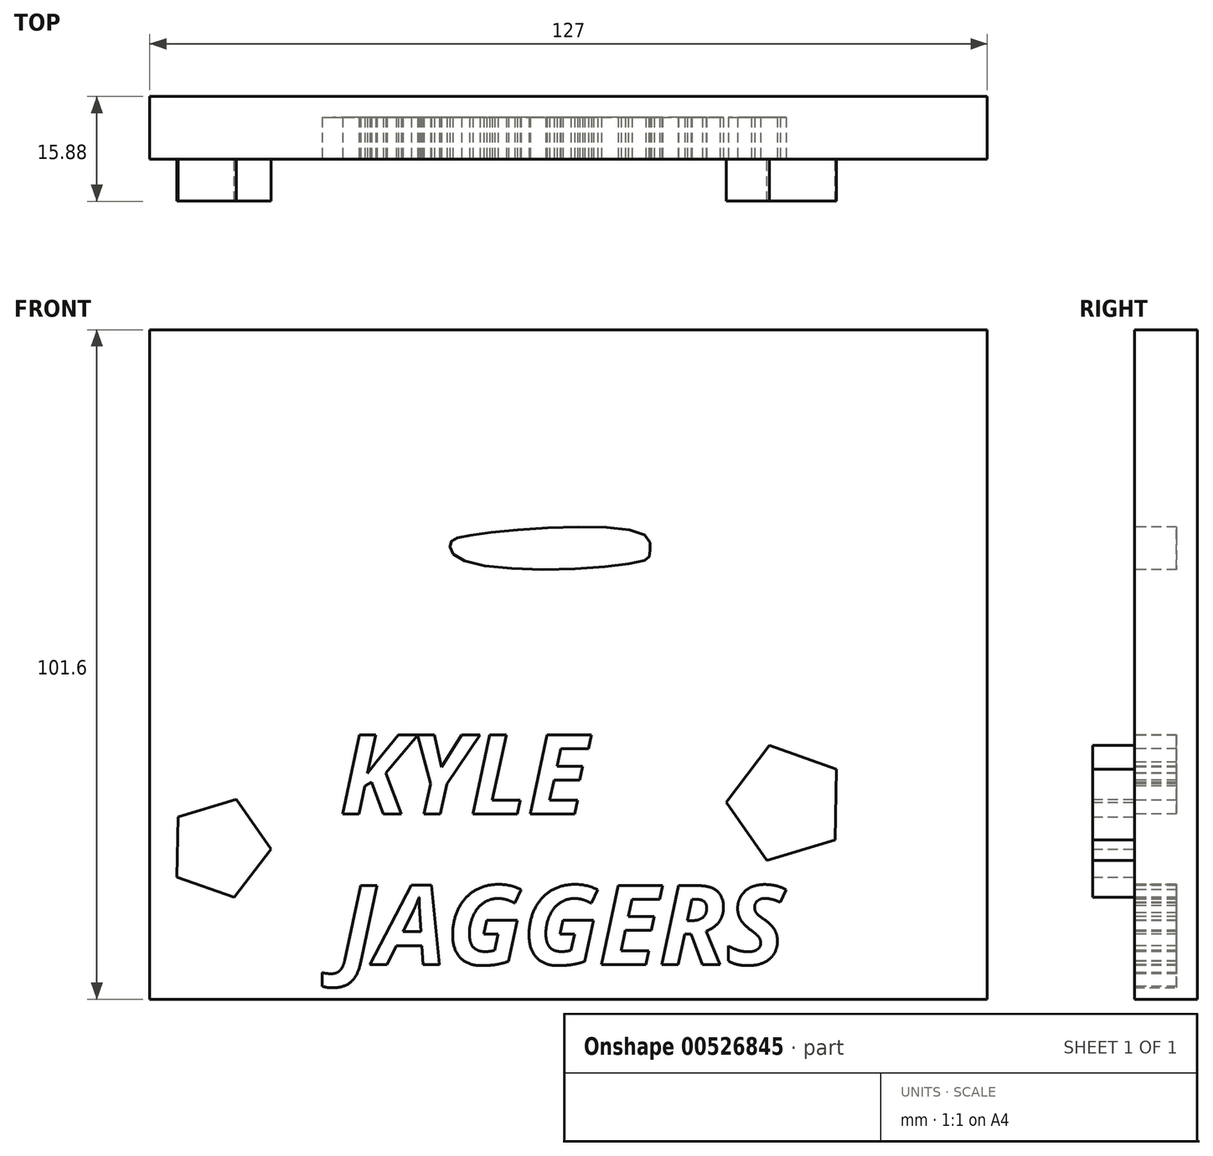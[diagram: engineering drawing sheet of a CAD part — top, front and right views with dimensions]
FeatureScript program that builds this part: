
annotation { "Feature Type Name" : "Feature", "Feature Type Description" : "" }
export const myFeature = defineFeature(function(context is Context, id is Id, definition is map)
    precondition{}
    {
        {
            var Q0;
            Q0=qCreatedBy(makeId("Front.planeOp"),FACE);
            var sketch = newSketch(context, id + "F0", { "sketchPlane" : qUnion([Q0])});
            skLineSegment(sketch, "E0.bottom", {"start": v(-61.05, 53.94) * mm, "end": v(65.95, 53.94) * mm});
            skLineSegment(sketch, "E0.top", {"start": v(-61.05, -47.66) * mm, "end": v(65.95, -47.66) * mm});
            skLineSegment(sketch, "E0.left", {"start": v(-61.05, 53.94) * mm, "end": v(-61.05, -47.66) * mm});
            skLineSegment(sketch, "E0.right", {"start": v(65.95, 53.94) * mm, "end": v(65.95, -47.66) * mm});
            skSolve(sketch);
        }
        {
            var Q0;
            Q0=makeQuery(id+"F0.imprint","IMPRINT",FACE,{"disambiguationData":[TD([[makeQuery(id+"F0.imprint","IMPRINT",EDGE,{"derivedFrom":sQuery(id+"F0.wireOp",EDGE,"E0.bottom")}),-1.0]])]});
            var Q1;
            Q1 = qSketchRegion(id + "F2", true);
            extrude(context, id + "F1", {"entities" : qUnion([Q0, Q1]), "depth" : 9.52 * mm, "offsetDistance" : 25.4 * mm});
        }
        {
            var Q0;
            Q0=makeQuery(id+"F1.opExtrude","CAP_FACE",FACE,{"disambiguationData":[OSD([sQuery(id+"F0.wireOp",EDGE,"E0.bottom"),sQuery(id+"F0.wireOp",EDGE,"E0.top"),sQuery(id+"F0.wireOp",EDGE,"E0.left"),sQuery(id+"F0.wireOp",EDGE,"E0.right")])],"isStart":false});
            var sketch = newSketch(context, id + "F2", { "sketchPlane" : qUnion([Q0])});
            skSolve(sketch);
        }
        {
            var Q0;
            Q0=makeQuery(id+"F2.imprint","IMPRINT",FACE,{"disambiguationData":[TD([[makeQuery(id+"F2.imprint","IMPRINT",EDGE,{"derivedFrom":makeQuery(id+"F1.opExtrude","CAP_EDGE",EDGE,{"disambiguationData":[OSD([sQuery(id+"F0.wireOp",EDGE,"E0.bottom")])],"isStart":false})}),-1.0]])]});
            var sketch = newSketch(context, id + "F3", { "sketchPlane" : qUnion([Q0])});
            skText(sketch, "E1", { "text": "KYLE\nJAGGERS", "fontName": "NotoSans-BoldItalic.ttf"});
            const initialGuessF3  = {"E1": [-0.03223, -0.01957, 1, 0, 0.01209]};
            skSetInitialGuess(sketch, initialGuessF3);
            skSolve(sketch);
        }
        {
            var Q0;
            Q0 = qSketchRegion(id + "F3", true);
            extrude(context, id + "F4", {"entities" : qUnion([Q0]), "operationType" : NewBodyOperationType.REMOVE, "oppositeDirection" : true, "depth" : 6.35 * mm, "offsetDistance" : 25.4 * mm});
        }
        {
            var Q0;
            Q0=makeQuery(id+"F2.imprint","IMPRINT",FACE,{"disambiguationData":[TD([[makeQuery(id+"F2.imprint","IMPRINT",EDGE,{"derivedFrom":makeQuery(id+"F1.opExtrude","CAP_EDGE",EDGE,{"disambiguationData":[OSD([sQuery(id+"F0.wireOp",EDGE,"E0.bottom")])],"isStart":false})}),-1.0]])]});
            var sketch = newSketch(context, id + "F5", { "sketchPlane" : qUnion([Q0])});
            skFitSpline(sketch, "E2", {"points": [v(-44.27, 33.78) * mm, v(-40.54, 29.16) * mm, v(-36.8, 25.96) * mm, v(-31.83, 22.76) * mm, v(-28.45, 20.8) * mm, v(-30.23, 20.45) * mm, v(-38.23, 15.47) * mm, v(-44.1, 8.36) * mm, v(-45.52, 3.02) * mm, v(-43.38, 1.96) * mm, v(-40.36, 0) * mm, v(-30.76, -3.73) * mm, v(-22.58, -5.33) * mm, v(-20.62, -5.16) * mm, v(-20.8, 1.78) * mm, v(-20.45, 12.45) * mm, v(-18.67, 17.6) * mm, v(-17.42, 17.42) * mm, v(-13.7, 16.36) * mm, v(-5.16, 15.3) * mm, v(6.58, 15.65) * mm, v(18.85, 17.42) * mm, v(19.56, 15.65) * mm, v(21.7, 11.73) * mm, v(21.16, 7.82) * mm, v(20.98, -5.51) * mm, v(22.76, -5.33) * mm, v(27.74, -4.45) * mm, v(44.98, 1.96) * mm, v(41.43, 12.45) * mm, v(34.32, 18.31) * mm, v(29.87, 20.98) * mm, v(30.94, 21.87) * mm, v(40.18, 27.91) * mm, v(46.05, 38.23) * mm, v(43.03, 40.9) * mm, v(28.45, 46.58) * mm, v(21.7, 47.47) * mm, v(20.98, 41.43) * mm, v(21.34, 31.83) * mm, v(18.31, 24.54) * mm, v(14.76, 25.6) * mm, v(3.02, 26.85) * mm, v(-12.45, 25.78) * mm, v(-17.96, 24.36) * mm, v(-20.27, 28.63) * mm, v(-20.8, 40.54) * mm, v(-20.8, 47.3) * mm, v(-26.31, 46.94) * mm, v(-34.5, 45.16) * mm, v(-44.8, 39.65) * mm, v(-44.27, 33.78) * mm]});
            skSolve(sketch);
        }
        {
            var Q0;
            Q0=makeQuery(id+"F5.imprint","IMPRINT",FACE,{"disambiguationData":[TD([[makeQuery(id+"F5.imprint","IMPRINT",EDGE,{"derivedFrom":sQuery(id+"F5.wireOp",EDGE,"E2")}),-1.0]])]});
            var sketch = newSketch(context, id + "F6", { "sketchPlane" : qUnion([Q0])});
            skSolve(sketch);
        }
        {
            var Q0;
            Q0=sQuery(id+"F5.wireOp",EDGE,"E2");
            var Q1;
            Q1 = qConstructionFilter(qBodyType(qCreatedBy(id + "F6" ,EDGE), BodyType.WIRE), ConstructionObject.NO);
            extrude(context, id + "F7", {"bodyType" : ToolBodyType.SURFACE, "surfaceEntities" : qUnion([Q0, Q1]), "depth" : 6.35 * mm, "offsetDistance" : 25.4 * mm});
        }
        {
            var Q0;
            Q0=makeQuery(id+"F6.imprint","IMPRINT",FACE,{"disambiguationData":[TD([[makeQuery(id+"F6.imprint","IMPRINT",EDGE,{"derivedFrom":makeQuery(id+"F5.imprint","IMPRINT",EDGE,{"derivedFrom":sQuery(id+"F5.wireOp",EDGE,"E2")})}),1.0]])]});
            var sketch = newSketch(context, id + "F8", { "sketchPlane" : qUnion([Q0])});
            skFitSpline(sketch, "E3", {"points": [v(-12.45, 22.76) * mm, v(-15.47, 21.51) * mm, v(-13.34, 18.85) * mm, v(14.22, 19.02) * mm, v(14.76, 20.1) * mm, v(14.05, 22.76) * mm, v(-12.45, 22.76) * mm]});
            skSolve(sketch);
        }
        {
            var Q0;
            Q0=makeQuery(id+"F8.imprint","IMPRINT",FACE,{"disambiguationData":[TD([[makeQuery(id+"F8.imprint","IMPRINT",EDGE,{"derivedFrom":sQuery(id+"F8.wireOp",EDGE,"E3")}),1.0]])]});
            var Q1;
            Q1=sQuery(id+"F8.wireOp",EDGE,"E3");
            extrude(context, id + "F9", {"entities" : qUnion([Q0]), "operationType" : NewBodyOperationType.REMOVE, "surfaceEntities" : qUnion([Q1]), "oppositeDirection" : true, "depth" : 6.35 * mm, "offsetDistance" : 25.4 * mm});
        }
        {
            var Q0;
            Q0=makeQuery(id+"F6.imprint","IMPRINT",FACE,{"disambiguationData":[TD([[makeQuery(id+"F6.imprint","IMPRINT",EDGE,{"derivedFrom":makeQuery(id+"F5.imprint","IMPRINT",EDGE,{"derivedFrom":sQuery(id+"F5.wireOp",EDGE,"E2")})}),-1.0]])]});
            var sketch = newSketch(context, id + "F10", { "sketchPlane" : qUnion([Q0])});
            skCircle(sketch, "E4.cCircle", {"center": v(35.56, -17.96) * mm, "radius": 7.43 * mm, "construction": true});
            skLineSegment(sketch, "E4.0", {"start": v(42.86, -23.52) * mm, "end": v(32.53, -26.62) * mm});
            skLineSegment(sketch, "E4.1", {"start": v(32.53, -26.62) * mm, "end": v(26.38, -17.75) * mm});
            skLineSegment(sketch, "E4.2", {"start": v(26.38, -17.75) * mm, "end": v(32.92, -9.17) * mm});
            skLineSegment(sketch, "E4.3", {"start": v(32.92, -9.17) * mm, "end": v(43.1, -12.73) * mm});
            skLineSegment(sketch, "E4.4", {"start": v(43.1, -12.73) * mm, "end": v(42.86, -23.52) * mm});
            skPoint(sketch, "E4.0.midPoint", {"position": v(37.7, -25.07) * mm});
            skCircle(sketch, "E5.cCircle", {"center": v(-50.5, -24.71) * mm, "radius": 6.33 * mm, "construction": true});
            skLineSegment(sketch, "E5.0", {"start": v(-42.67, -24.9) * mm, "end": v(-48.25, -32.2) * mm});
            skLineSegment(sketch, "E5.1", {"start": v(-48.25, -32.2) * mm, "end": v(-56.93, -29.17) * mm});
            skLineSegment(sketch, "E5.2", {"start": v(-56.93, -29.17) * mm, "end": v(-56.72, -19.97) * mm});
            skLineSegment(sketch, "E5.3", {"start": v(-56.72, -19.97) * mm, "end": v(-47.9, -17.33) * mm});
            skLineSegment(sketch, "E5.4", {"start": v(-47.9, -17.33) * mm, "end": v(-42.67, -24.9) * mm});
            skPoint(sketch, "E5.0.midPoint", {"position": v(-45.46, -28.55) * mm});
            skSolve(sketch);
        }
        {
            var Q0;
            Q0 = qSketchRegion(id + "F10", true);
            extrude(context, id + "F11", {"entities" : qUnion([Q0]), "operationType" : NewBodyOperationType.ADD, "depth" : 6.35 * mm, "offsetDistance" : 25.4 * mm});
        }
    });
